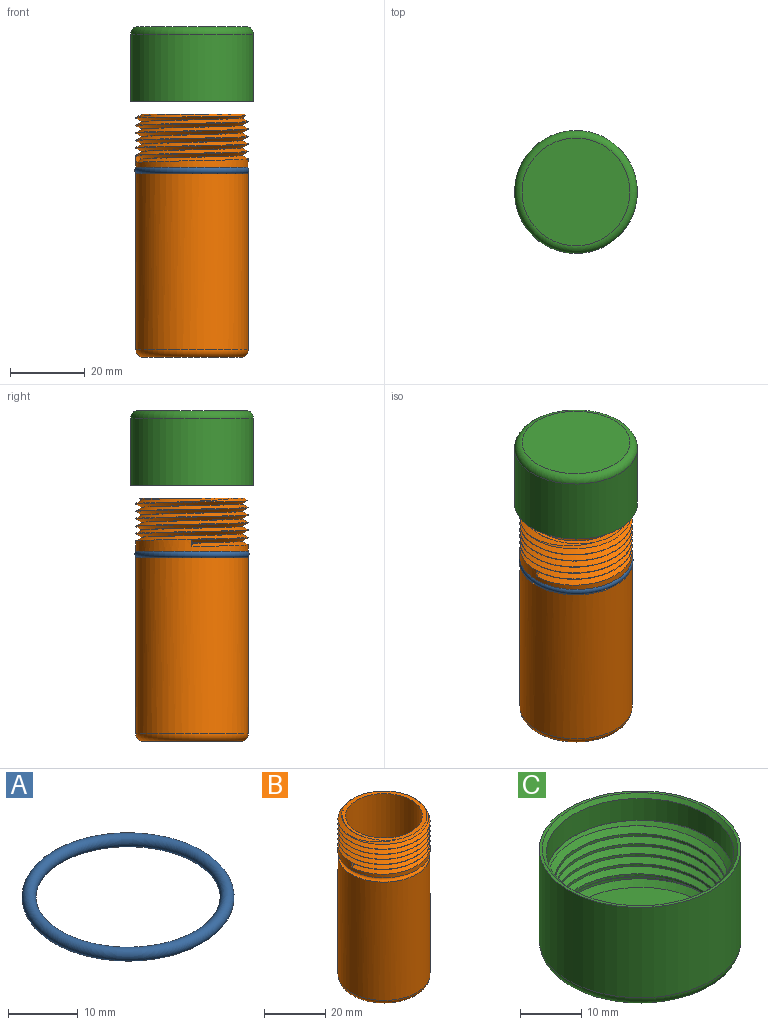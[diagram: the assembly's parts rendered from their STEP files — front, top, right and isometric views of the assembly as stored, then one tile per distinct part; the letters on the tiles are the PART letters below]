
ASSEMBLY  parts=3 mates=4
PART A: 1 faces, bbox 33x33x2 mm
  f0: torus R=14.25mm, axis (0,0,1), area 562.6mm2
PART B: 20 faces, bbox 33.1x35x66.1 mm
  f0: cylinder r=15mm len=30mm, axis (0,0,-1), area 10.9mm2, adj f1,f6,f13,f15
  f1: cylinder r=15mm len=30mm, axis (0,0,-1), area 10.9mm2, adj f0,f2,f13,f15
  f2: cylinder r=15mm len=30mm, axis (0,0,-1), area 11mm2, adj f1,f3,f13,f15
  f3: cylinder r=15mm len=30mm, axis (0,0,-1), area 10.9mm2, adj f2,f4,f13,f15
  f4: cylinder r=15mm len=30mm, axis (0,0,-1), area 10.8mm2, adj f3,f5,f11,f13,f15
  f5: cylinder r=15mm len=2.85mm, axis (0,0,-1), area 0.1mm2, adj f4,f11,f13
  f6: cylinder r=15mm len=30mm, axis (0,0,-1), area 206.6mm2, adj f0,f12,f15,f16
  f7: plane 28.15x27.62mm, normal (0,0,1), area 115.2mm2, adj f8,f11,f13,f14,f15
  f8: cylinder r=12.5mm len=60.5mm, axis (0,0,-1), area 4751.7mm2, adj f7,f10
  f9: plane 21x21mm, normal (0,0,1), area 346.4mm2, adj f10
  f10: torus R=10.5mm, axis (0,0,1), area 232.4mm2, adj f8,f9
  f11: cone r=14mm half-angle=45deg, axis (0,0,-1), area 44.3mm2, adj f4,f5,f7,f13,f15
  f12: plane 1.89x1.54mm, normal (0,-1,0), area 1.5mm2, adj f6,f13,f14,f15
  f13: bspline ~34.87x30.2mm, area 853.7mm2, adj f0,f1,f2,f3,f4,f5,f7,f11
  f14: bspline ~31.22x27.04mm, area 106.4mm2, adj f7,f12,f13,f15
  f15: bspline ~34.87x30.2mm, area 933.5mm2, adj f0,f1,f2,f3,f4,f6,f7,f11
  f16: torus R=14.5mm, axis (0,0,-1), area 370.7mm2, adj f6,f19
  f17: plane 26x26mm, normal (0,0,-1), area 530.9mm2, adj f18
  f18: torus R=13mm, axis (0,0,1), area 281.7mm2, adj f17,f19
  f19: cylinder r=15mm len=47.13mm, axis (0,0,-1), area 4442.3mm2, adj f16,f18
PART C: 18 faces, bbox 35.5x35.5x20 mm
  f0: cylinder r=13.92mm len=27.84mm, axis (0,0,-1), area 201.2mm2, adj f3,f11,f15,f17
  f1: cylinder r=15mm len=20.63mm, axis (0,0,-1), area 9.2mm2, adj f2,f3,f15
  f2: cylinder r=15mm len=30mm, axis (0,0,-1), area 76.2mm2, adj f1,f3,f12,f14,f17
  f3: plane 30x30mm, normal (0,0,-1), area 55.7mm2, adj f0,f1,f2,f15,f17
  f4: plane 28x28mm, normal (0,0,1), area 615.8mm2, adj f12
  f5: cylinder r=15.25mm len=30.5mm, axis (0,0,1), area 415.1mm2, adj f6,f10
  f6: plane 30.5x30.5mm, normal (0,0,1), area 3.1mm2, adj f5,f11
  f7: plane 28.84x28.84mm, normal (0,0,-1), area 653mm2, adj f13
  f8: cylinder r=16.42mm len=32.84mm, axis (0,0,-1), area 1856.8mm2, adj f9,f13
  f9: plane 32.84x32.84mm, normal (0,0,1), area 50.8mm2, adj f8,f10
  f10: cone r=13.92mm half-angle=45deg, axis (0,0,1), area 92.4mm2, adj f5,f9
  f11: cone r=13.92mm half-angle=45deg, axis (0,0,1), area 106.3mm2, adj f0,f6,f15,f16,f17
  f12: cone r=14mm half-angle=45deg, axis (0,0,1), area 128.8mm2, adj f2,f4
  f13: torus R=14.42mm, axis (0,0,1), area 309.7mm2, adj f7,f8
  f14: plane 0.25x0.17mm, normal (0,1,0), area 0mm2, adj f2,f15,f16,f17
  f15: bspline ~34.97x30.28mm, area 638.4mm2, adj f0,f1,f3,f11,f14,f16
  f16: bspline ~35.05x30.36mm, area 55.8mm2, adj f11,f14,f15,f17
  f17: bspline ~34.97x30.28mm, area 640.9mm2, adj f0,f2,f3,f11,f14,f16
PLACE A rot(axis=(0,0,-1),180deg) t=(33.92,23.15,-64.12)mm
PLACE B t=(33.92,23.15,-114.12)mm
PLACE C rot(axis=(1,0,0),180deg) t=(33.92,23.15,-25.72)mm
MATE cylindrical C.f0 <-> B.f0  axis (0,0,1) through (33.92,23.15,-36.72)mm
MATE cylindrical A.f0 <-> B.f0  axis (0,0,1) through (33.92,23.15,-64.12)mm
MATE parallel B.f7 <-> C.f1  axis (0,0,1) through (34.95,23.15,-49.12)mm
MATE cylindrical A.f0 <-> B.f0  axis (0,0,1) through (33.92,23.15,-64.12)mm
